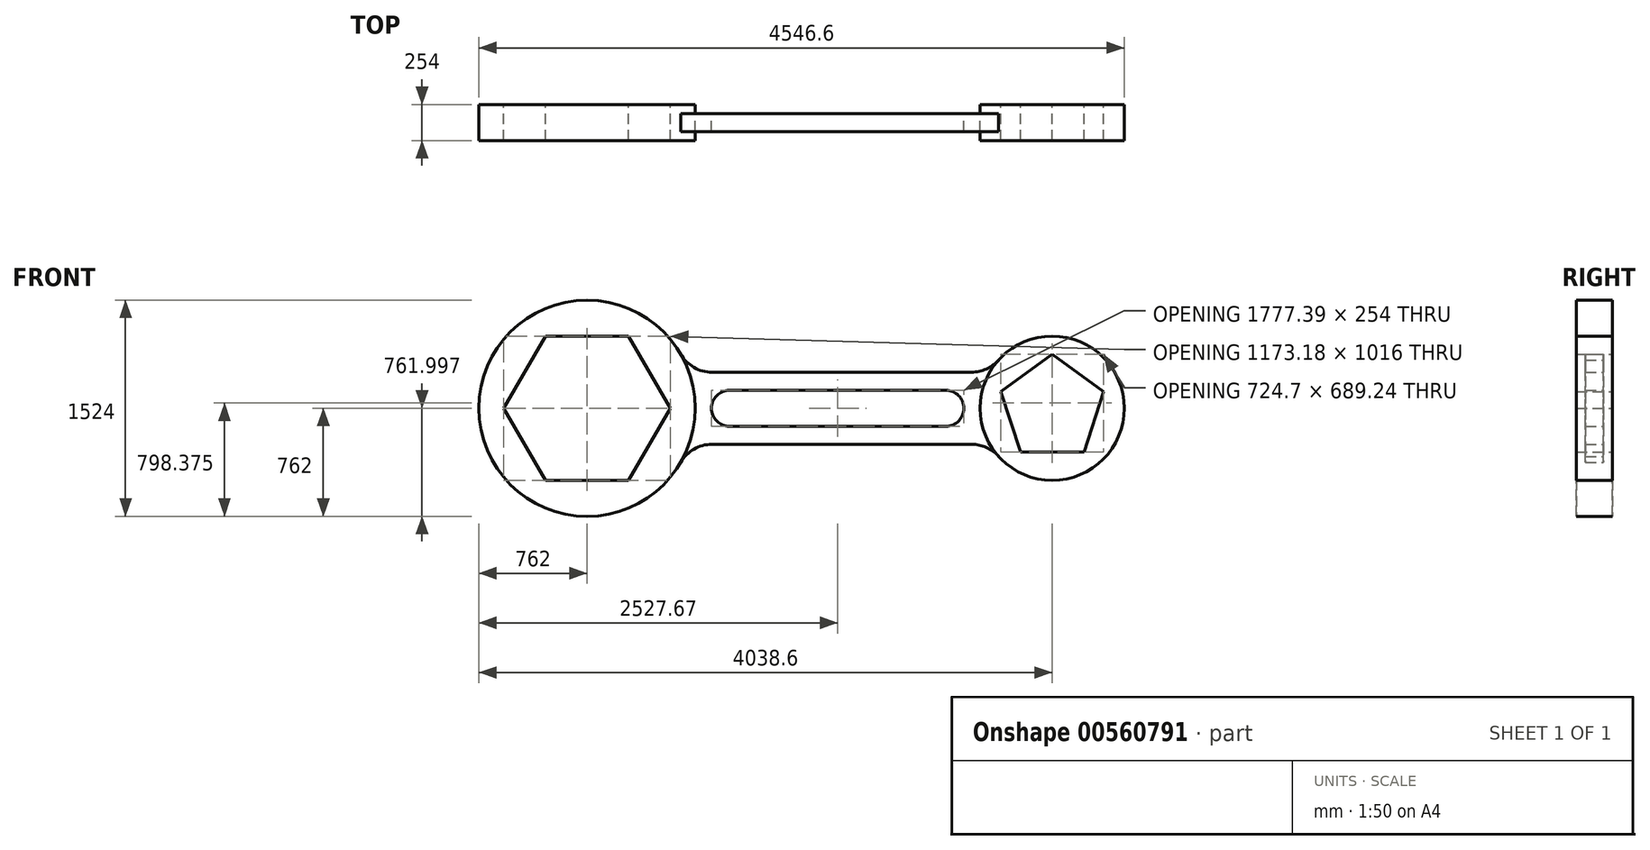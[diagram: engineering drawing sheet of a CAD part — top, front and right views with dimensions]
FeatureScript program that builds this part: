
annotation { "Feature Type Name" : "Feature", "Feature Type Description" : "" }
export const myFeature = defineFeature(function(context is Context, id is Id, definition is map)
    precondition{}
    {
        {
            var Q0;
            Q0=qCreatedBy(makeId("Front.planeOp"),FACE);
            var sketch = newSketch(context, id + "F0", { "sketchPlane" : qUnion([Q0])});
            skCircle(sketch, "E0", {"center": v(0, 0) * mm, "radius": 762 * mm});
            skCircle(sketch, "E1", {"center": v(3276.6, 0) * mm, "radius": 508 * mm});
            skLineSegment(sketch, "E2", {"start": v(762, 0) * mm, "end": v(2768.6, 0) * mm});
            skLineSegment(sketch, "E3", {"start": v(1765.3, 0) * mm, "end": v(1765.3, 127) * mm});
            skLineSegment(sketch, "E4", {"start": v(1765.3, 127) * mm, "end": v(1003.33, 127) * mm});
            skLineSegment(sketch, "E5", {"start": v(1003.97, -127) * mm, "end": v(2528.27, -127) * mm});
            skLineSegment(sketch, "E6", {"start": v(2527.37, 127) * mm, "end": v(1765.3, 127) * mm});
            skArc(sketch, "E7", {"start": v(1003.33, 127) * mm, "mid": v(876.97, -0.32) * mm, "end": v(1003.97, -127) * mm});
            skLineSegment(sketch, "E8", {"start": v(1765.3, 0) * mm, "end": v(1765.3, 254) * mm});
            skLineSegment(sketch, "E9", {"start": v(1765.3, 0) * mm, "end": v(1765.3, -254) * mm});
            skPoint(sketch, "E9.endSnap0", {"position": v(1765.3, -127) * mm});
            skLineSegment(sketch, "E10", {"start": v(1765.3, 254) * mm, "end": v(879.88, 254) * mm});
            skLineSegment(sketch, "E11", {"start": v(1765.3, 254) * mm, "end": v(2708.64, 254) * mm});
            skLineSegment(sketch, "E12", {"start": v(1765.3, -254) * mm, "end": v(879.88, -254) * mm});
            skLineSegment(sketch, "E13", {"start": v(1765.3, -254) * mm, "end": v(2708.64, -254) * mm});
            skArc(sketch, "E14", {"start": v(659.91, 381) * mm, "mid": v(752.88, 288.03) * mm, "end": v(879.88, 254) * mm});
            skArc(sketch, "E15", {"start": v(2708.64, 254) * mm, "mid": v(2812.34, 276.13) * mm, "end": v(2897.96, 338.66) * mm});
            skArc(sketch, "E16", {"start": v(2897.96, -338.67) * mm, "mid": v(2812.33, -276.13) * mm, "end": v(2708.64, -254) * mm});
            skArc(sketch, "E17", {"start": v(879.88, -254) * mm, "mid": v(752.88, -288.03) * mm, "end": v(659.9, -381) * mm});
            skPoint(sketch, "E18.orphan", {"position": v(876.97, -127) * mm});
            skArc(sketch, "E19", {"start": v(2528.27, -127) * mm, "mid": v(2654.36, 0.45) * mm, "end": v(2527.37, 127) * mm});
            skPoint(sketch, "E20.orphan", {"position": v(2653.63, -127) * mm});
            skCircle(sketch, "E21.cCircle", {"center": v(0, 0) * mm, "radius": 508 * mm, "construction": true});
            skLineSegment(sketch, "E21.0", {"start": v(-293.3, 508) * mm, "end": v(293.3, 508) * mm});
            skLineSegment(sketch, "E21.1", {"start": v(293.3, 508) * mm, "end": v(586.59, 0) * mm});
            skLineSegment(sketch, "E21.2", {"start": v(586.59, 0) * mm, "end": v(293.3, -508) * mm});
            skLineSegment(sketch, "E21.3", {"start": v(293.3, -508) * mm, "end": v(-293.3, -508) * mm});
            skLineSegment(sketch, "E21.4", {"start": v(-293.3, -508) * mm, "end": v(-586.59, 0) * mm});
            skLineSegment(sketch, "E21.5", {"start": v(-586.59, 0) * mm, "end": v(-293.3, 508) * mm});
            skPoint(sketch, "E21.0.midPoint", {"position": v(0, 508) * mm});
            skCircle(sketch, "E22.cCircle", {"center": v(3276.6, 0) * mm, "radius": 308.24 * mm, "construction": true});
            skLineSegment(sketch, "E22.0", {"start": v(3500.55, -308.24) * mm, "end": v(3052.65, -308.24) * mm});
            skLineSegment(sketch, "E22.1", {"start": v(3052.65, -308.24) * mm, "end": v(2914.25, 117.73) * mm});
            skLineSegment(sketch, "E22.2", {"start": v(2914.25, 117.73) * mm, "end": v(3276.6, 381) * mm});
            skLineSegment(sketch, "E22.3", {"start": v(3276.6, 381) * mm, "end": v(3638.95, 117.73) * mm});
            skLineSegment(sketch, "E22.4", {"start": v(3638.95, 117.73) * mm, "end": v(3500.55, -308.24) * mm});
            skPoint(sketch, "E22.0.midPoint", {"position": v(3276.6, -308.24) * mm});
            skSolve(sketch);
        }
        {
            var Q0;
            Q0=makeQuery(id+"F0.imprint","IMPRINT",FACE,{"disambiguationData":[TD([[makeQuery(id+"F0.imprint","IMPRINT",EDGE,{"derivedFrom":sQuery(id+"F0.wireOp",EDGE,"E21.0")}),1.0]])]});
            var Q1;
            Q1=makeQuery(id+"F0.imprint","IMPRINT",FACE,{"disambiguationData":[TD([[makeQuery(id+"F0.imprint","IMPRINT",EDGE,{"derivedFrom":sQuery(id+"F0.wireOp",EDGE,"E22.0")}),1.0]])]});
            extrude(context, id + "F1", {"entities" : qUnion([Q0, Q1]), "depth" : 254 * mm, "offsetDistance" : 25.4 * mm, "symmetric" : true});
        }
        {
            var Q0;
            {var subQ9=sQuery(id+"F0.wireOp",EDGE,"E12");Q0=makeQuery(id+"F0.imprint","IMPRINT",FACE,{"disambiguationData":[TD([[makeQuery(id+"F0.imprint","IMPRINT",EDGE,{"derivedFrom":subQ9}),-1.0]])]});}
            var Q1;
            {var subQ10=sQuery(id+"F0.wireOp",EDGE,"E10");Q1=makeQuery(id+"F0.imprint","IMPRINT",FACE,{"disambiguationData":[TD([[makeQuery(id+"F0.imprint","IMPRINT",EDGE,{"derivedFrom":subQ10}),1.0]])]});}
            var Q2;
            {var subQ0=sQuery(id+"F0.wireOp",EDGE,"E6");Q2=makeQuery(id+"F0.imprint","IMPRINT",FACE,{"disambiguationData":[TD([[makeQuery(id+"F0.imprint","IMPRINT",EDGE,{"derivedFrom":subQ0}),-1.0]])]});}
            var Q3;
            {var subQ0=sQuery(id+"F0.wireOp",EDGE,"E13");Q3=makeQuery(id+"F0.imprint","IMPRINT",FACE,{"disambiguationData":[TD([[makeQuery(id+"F0.imprint","IMPRINT",EDGE,{"derivedFrom":subQ0}),1.0]])]});}
            extrude(context, id + "F2", {"entities" : qUnion([Q0, Q1, Q2, Q3]), "depth" : 127 * mm, "offsetDistance" : 25.4 * mm, "symmetric" : true});
        }
    });
